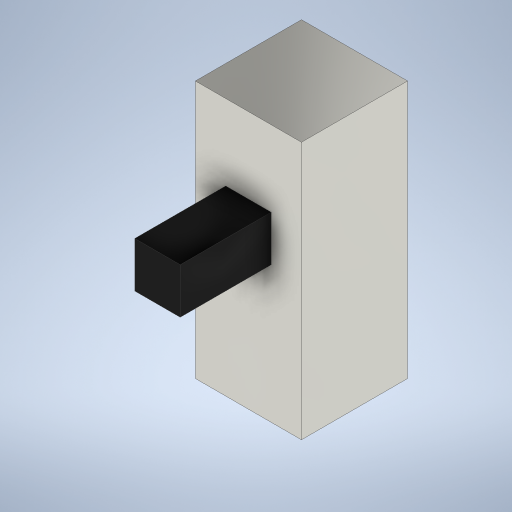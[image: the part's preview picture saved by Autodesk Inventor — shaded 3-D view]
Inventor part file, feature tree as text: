
AUTODESK INVENTOR PART (.ipt)
format: ipt  version: 2024.3 (Build 283343000, 343)  size: 235,008 bytes
history: native  units: mm
features: extrude x2, sketch x2
ambient origin geometry x8: Origin, YZ Plane, XZ Plane, XY Plane, X Axis, Y Axis, Z Axis, Center Point
bodies: Solid1 (feature_tree)
feature tree (4):
  extrude  "Extrusion1"  Depth=8.5mm
  extrude  "Extrusion2"  Depth=1.5mm
  sketch  "Sketch1"  dims[d0=3.5mm d1=8.5mm]
  sketch  "Sketch2"  dims[d2=3.5mm d3=0.0mm d4=1.5mm d5=1.5mm d6=4.0mm d7=3.0mm d8=0.0mm]
